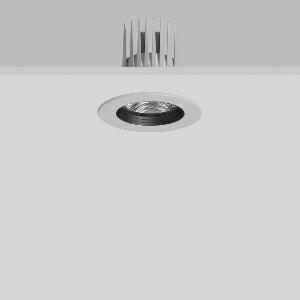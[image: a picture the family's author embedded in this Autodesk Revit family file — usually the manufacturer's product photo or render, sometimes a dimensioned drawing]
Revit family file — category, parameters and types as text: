
# Revit family: heledon_mini_e_901750_004_6da5
name_source: partatom
category: Lighting Fixtures
units: mm (PartAtom-declared; Revit-internal decimal feet)

## family parameters
Cut with Voids When Loaded = No
Host = Face
Light Source = No
Part Type = Normal
Room Calculation Point = No
Round Connector Dimension = Use Diameter
Shared = No

## types (1)
- HELEDON mini E (1 x LED Modul 930, 3650 lm, 3000)
    Apparent Load = 29 VA
    Approval mark = CE
    CIE Flux Codes = 95 99 100 100 100
    Color Rendering = 90
    Color Temperature = 3000
    Default Elevation = 1800 mm
    Description = Series: HELEDON mini
Round recessed downlight. Housing: die-cast aluminium, powder-coated. Black plastic ring and recessed LED to prevent glare from the side. Optical assembly with reflector made of MIRO-Silver with 98% total light reflection for outstanding efficiency - can be changed without tools. Best colour rendering index Ra>90. Suitable for Recessed ceiling mounting. Installation without tools thanks to spring fastening system. Including separate LED converter with connecting cable 600 mm.High quality converter without flickering and stroboscopic effect. Through-wiring box (5 pole) available as accessory. The following accessories can be mounted without use of tools: interchangeable lenses, decorative glasses, honeycomb louvre, clear and frosted diffusers, white interchangeable plastic ring. 
Colour: silver
Diameter: 124 mm
Height: 3 mm
Cut-out diameter: 114 mm
Recess height: 170 mm
Luminaire: recess height: 120 mm
Lamp: LED
Socket: without socket
Colour temperature: 3000K
Colour rendering index (CRI): 92
System power: 29 W
Rated luminous flux: 3650 lm
Luminous efficiency: 126 lm/W
Control gear: Regulated power supply
Protection class: II
Type of protection: IP 20
    Height = 0 mm  [stored 0 ft]
    Lamp = 1 x LED Modul 930
    Lamp Light Flux = 3650 lm
    Lamp count = 1
    Length = 124 mm  [stored 0.406824 ft]
    Lifetime = 50000 h
    Luminous efficacy = 126 lm/W
    Manufacturer = RZB
    ModVariant = No
    Model = 901750.004
    Mounting Place = Ceiling
    Mounting Type = Recessed
    Number of Poles = 1
    OnlyDefault = Yes
    Power Factor = 1
    Product Name = HELEDON mini E
    Product group = Recessed downlights
    ProductGroupID = 402
    Protection Class = Protection class II
    Protection Degree = IP 20
    RLX_Detail_Level = 1
    RLX_Emergency_Light_Flux = 0 lm
    RLX_Emergency_Type = 0
    RLX_Emergency_Type_DB = No
    RlxData = <blob elided: 125637 chars, md5=1f6360c3>
    Socket = socket
    Standby Power = 0 W
    System Light Flux = 3650 lm
    System Power = 29 W
    Type Comments = Product without accessories
    Type Image = 901657.004.jpg
    URL = http://relux.com
    VarID = ---
    Voltage = 230 V
    Voltage Range = 220-240 V
    Weight = 0.00 kg
    Width = 0 mm  [stored 0 ft]

note: [stored X ft] marks values corroborated as IEEE doubles in the binary element streams (Revit-internal decimal feet)

## geometry (parser evidence)
native form markers: Blend x4, Sweep x12
no freeform markers — native parametric forms only
